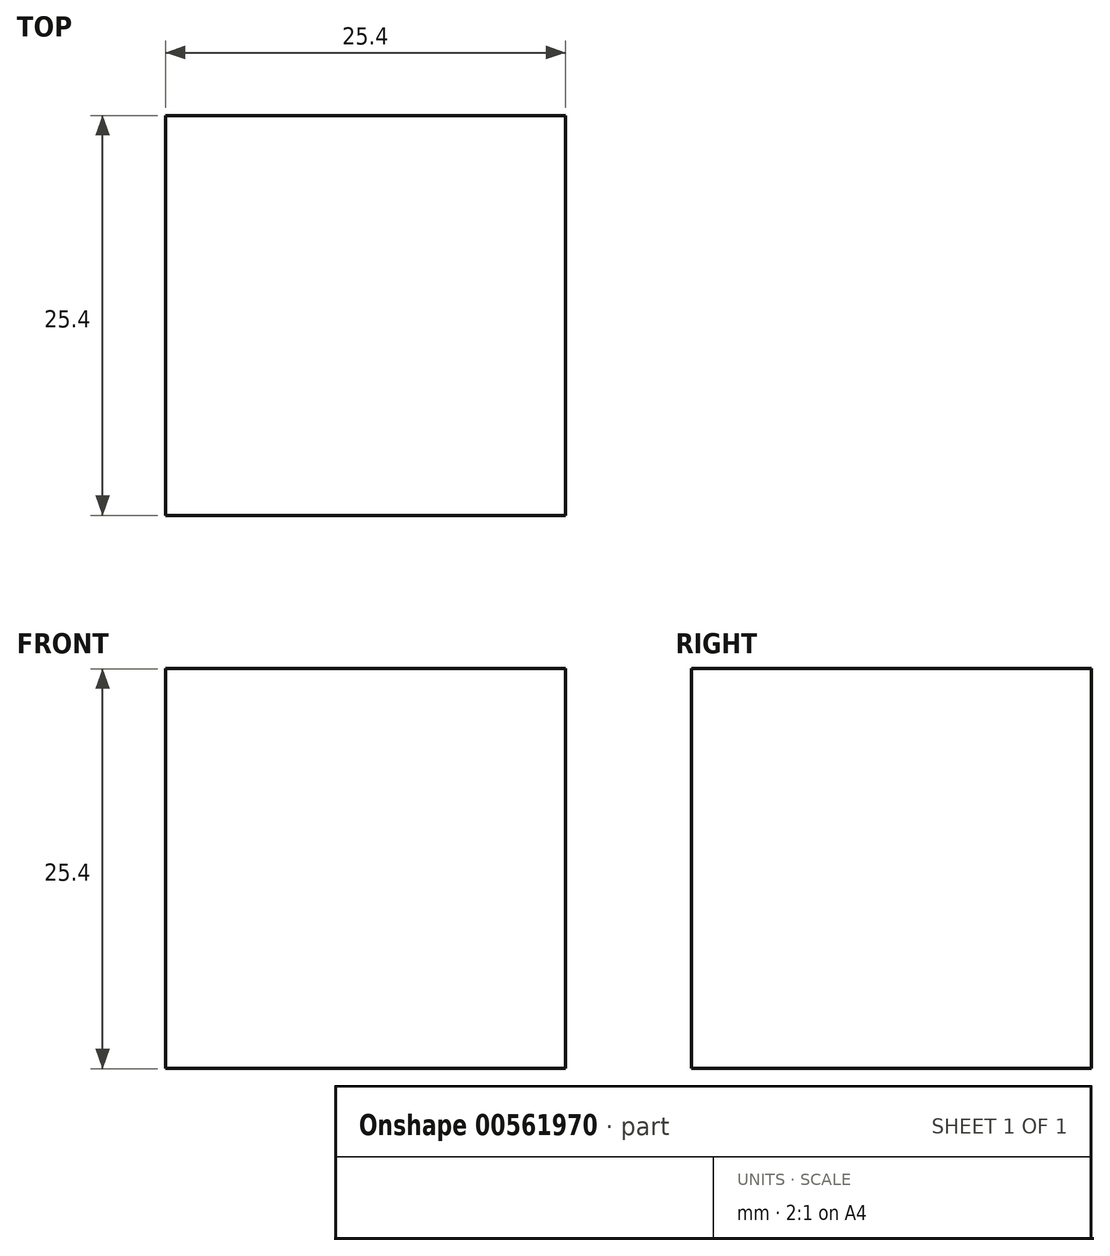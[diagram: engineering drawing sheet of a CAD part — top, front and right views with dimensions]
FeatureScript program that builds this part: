
annotation { "Feature Type Name" : "Feature", "Feature Type Description" : "" }
export const myFeature = defineFeature(function(context is Context, id is Id, definition is map)
    precondition{}
    {
        {
            var Q0;
            Q0=qCreatedBy(makeId("Front.planeOp"),FACE);
            var sketch = newSketch(context, id + "F0", { "sketchPlane" : qUnion([Q0])});
            skLineSegment(sketch, "E0.bottom", {"start": v(-51.4, 53.66) * mm, "end": v(-26, 53.66) * mm});
            skLineSegment(sketch, "E0.top", {"start": v(-51.4, 28.26) * mm, "end": v(-26, 28.26) * mm});
            skLineSegment(sketch, "E0.left", {"start": v(-51.4, 53.66) * mm, "end": v(-51.4, 28.26) * mm});
            skLineSegment(sketch, "E0.right", {"start": v(-26, 53.66) * mm, "end": v(-26, 28.26) * mm});
            skSolve(sketch);
        }
        {
            var Q0;
            Q0=makeQuery(id+"F0.imprint","IMPRINT",FACE,{"disambiguationData":[TD([[makeQuery(id+"F0.imprint","IMPRINT",EDGE,{"derivedFrom":sQuery(id+"F0.wireOp",EDGE,"E0.bottom")}),-1.0]])]});
            extrude(context, id + "F1", {"entities" : qUnion([Q0]), "depth" : 25.4 * mm, "offsetDistance" : 25.4 * mm});
        }
    });
